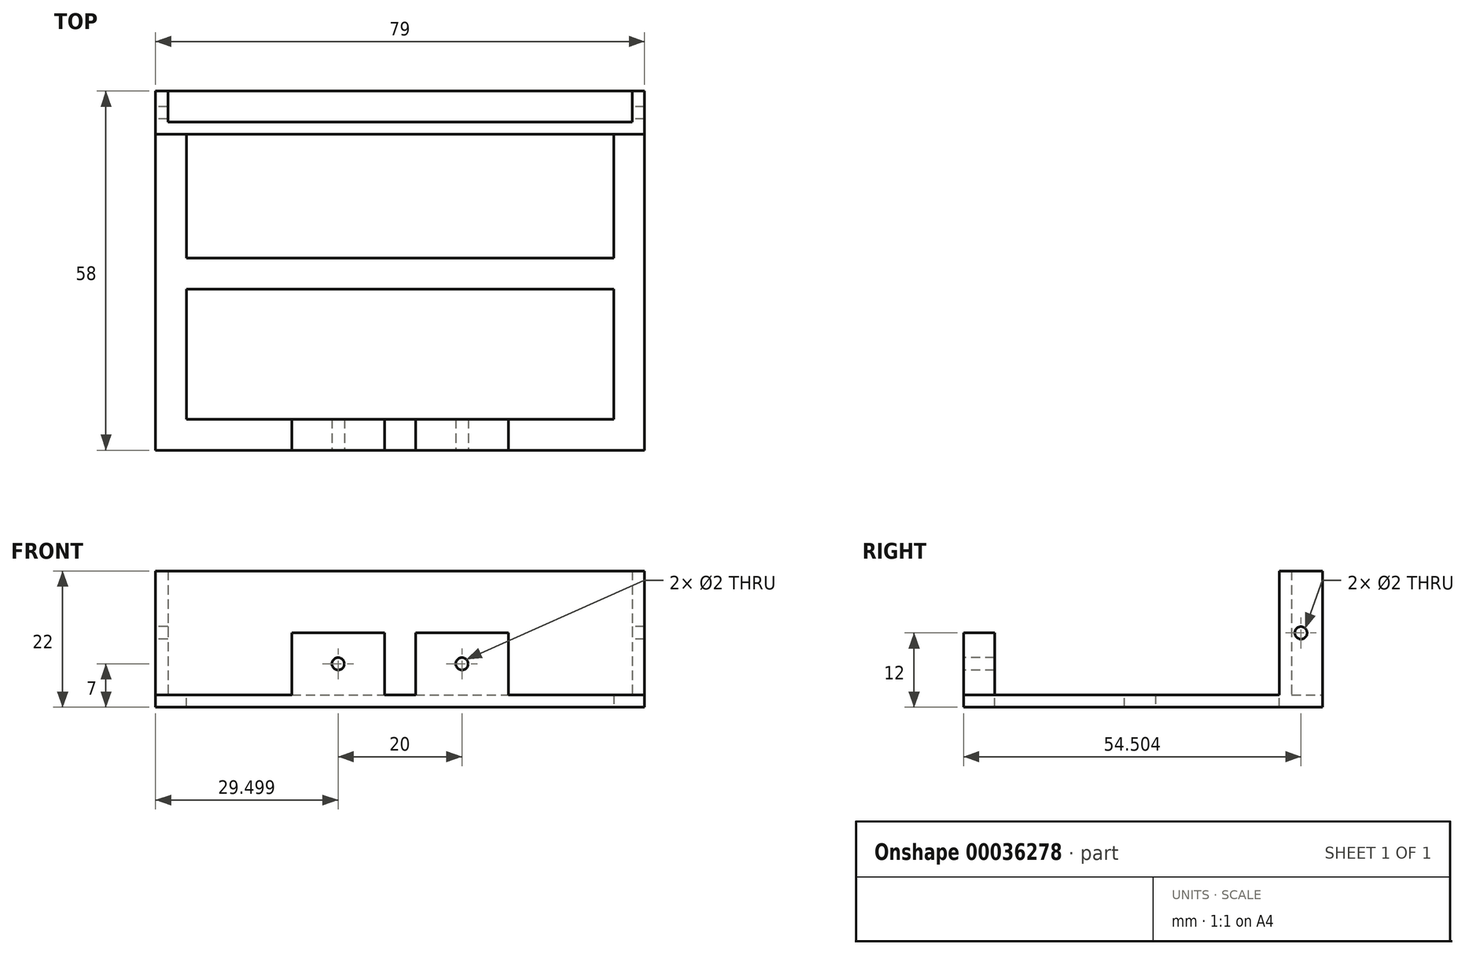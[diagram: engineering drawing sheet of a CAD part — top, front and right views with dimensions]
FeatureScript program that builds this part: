
annotation { "Feature Type Name" : "Feature", "Feature Type Description" : "" }
export const myFeature = defineFeature(function(context is Context, id is Id, definition is map)
    precondition{}
    {
        {
            var Q0;
            Q0=qCreatedBy(makeId("Top.planeOp"),FACE);
            var sketch = newSketch(context, id + "F0", { "sketchPlane" : qUnion([Q0])});
            skLineSegment(sketch, "E0.bottom", {"start": v(-44.08, 15.1) * mm, "end": v(34.92, 15.1) * mm});
            skLineSegment(sketch, "E0.top", {"start": v(-44.08, -42.9) * mm, "end": v(34.92, -42.9) * mm});
            skLineSegment(sketch, "E0.left", {"start": v(-44.08, 15.1) * mm, "end": v(-44.08, -42.9) * mm});
            skLineSegment(sketch, "E0.right", {"start": v(34.92, 15.1) * mm, "end": v(34.92, -42.9) * mm});
            skLineSegment(sketch, "E1.bottom", {"start": v(-39.08, 10.1) * mm, "end": v(29.92, 10.1) * mm});
            skLineSegment(sketch, "E1.top", {"start": v(-39.08, -35.9) * mm, "end": v(29.92, -35.9) * mm});
            skLineSegment(sketch, "E1.left", {"start": v(-39.08, 10.1) * mm, "end": v(-39.08, -35.9) * mm});
            skLineSegment(sketch, "E1.right", {"start": v(29.92, 10.1) * mm, "end": v(29.92, -35.9) * mm});
            skSolve(sketch);
        }
        {
            var Q0;
            Q0=makeQuery(id+"F0.imprint","IMPRINT",FACE,{"disambiguationData":[TD([[makeQuery(id+"F0.imprint","IMPRINT",EDGE,{"derivedFrom":sQuery(id+"F0.wireOp",EDGE,"E0.bottom")}),-1.0]])]});
            extrude(context, id + "F1", {"entities" : qUnion([Q0]), "depth" : 2 * mm});
        }
        {
            var Q0;
            Q0=makeQuery(id+"F1.opExtrude","CAP_FACE",FACE,{"disambiguationData":[OSD([sQuery(id+"F0.wireOp",EDGE,"E0.bottom"),sQuery(id+"F0.wireOp",EDGE,"E0.top"),sQuery(id+"F0.wireOp",EDGE,"E0.left"),sQuery(id+"F0.wireOp",EDGE,"E0.right"),sQuery(id+"F0.wireOp",EDGE,"E1.bottom"),sQuery(id+"F0.wireOp",EDGE,"E1.top"),sQuery(id+"F0.wireOp",EDGE,"E1.left"),sQuery(id+"F0.wireOp",EDGE,"E1.right")])],"isStart":true});
            var sketch = newSketch(context, id + "F2", { "sketchPlane" : qUnion([Q0])});
            skLineSegment(sketch, "E2.bottom", {"start": v(-22.08, -15.1) * mm, "end": v(-7.08, -15.1) * mm});
            skLineSegment(sketch, "E2.top", {"start": v(-22.08, -10.1) * mm, "end": v(-7.08, -10.1) * mm});
            skLineSegment(sketch, "E2.left", {"start": v(-22.08, -15.1) * mm, "end": v(-22.08, -10.1) * mm});
            skLineSegment(sketch, "E2.right", {"start": v(-7.08, -15.1) * mm, "end": v(-7.08, -10.1) * mm});
            skLineSegment(sketch, "E3.bottom", {"start": v(-2.08, -15.1) * mm, "end": v(12.92, -15.1) * mm});
            skLineSegment(sketch, "E3.top", {"start": v(-2.08, -10.1) * mm, "end": v(12.92, -10.1) * mm});
            skLineSegment(sketch, "E3.left", {"start": v(-2.08, -15.1) * mm, "end": v(-2.08, -10.1) * mm});
            skLineSegment(sketch, "E3.right", {"start": v(12.92, -15.1) * mm, "end": v(12.92, -10.1) * mm});
            skSolve(sketch);
        }
        {
            var Q0;
            Q0=makeQuery(id+"F2.imprint","IMPRINT",FACE,{"disambiguationData":[TD([[makeQuery(id+"F2.imprint","IMPRINT",EDGE,{"derivedFrom":sQuery(id+"F2.wireOp",EDGE,"E3.bottom")}),1.0]])]});
            var Q1;
            Q1=makeQuery(id+"F2.imprint","IMPRINT",FACE,{"disambiguationData":[TD([[makeQuery(id+"F2.imprint","IMPRINT",EDGE,{"derivedFrom":sQuery(id+"F2.wireOp",EDGE,"E2.bottom")}),1.0]])]});
            extrude(context, id + "F3", {"entities" : qUnion([Q0, Q1]), "operationType" : NewBodyOperationType.ADD, "depth" : 10 * mm});
        }
        {
            var Q0;
            {var subQ0=sQuery(id+"F0.wireOp",EDGE,"E0.bottom");var subQ1=sQuery(id+"F0.wireOp",EDGE,"E0.top");var subQ2=sQuery(id+"F0.wireOp",EDGE,"E0.left");var subQ3=sQuery(id+"F0.wireOp",EDGE,"E0.right");var subQ4=sQuery(id+"F0.wireOp",EDGE,"E1.bottom");var subQ5=sQuery(id+"F0.wireOp",EDGE,"E1.top");var subQ6=sQuery(id+"F0.wireOp",EDGE,"E1.left");var subQ7=sQuery(id+"F0.wireOp",EDGE,"E1.right");Q0=makeQuery(id+"F3.boolean.opBoolean","SPLIT",FACE,{"disambiguationData":[TD([makeQuery(id+"F1.opExtrude","SWEPT_FACE",FACE,{"disambiguationData":[OSD([subQ1])]})])],"derivedFrom":makeQuery(id+"F1.opExtrude","CAP_FACE",FACE,{"disambiguationData":[OSD([subQ0,subQ1,subQ2,subQ3,subQ4,subQ5,subQ6,subQ7])],"isStart":true})});}
            var sketch = newSketch(context, id + "F4", { "sketchPlane" : qUnion([Q0])});
            skLineSegment(sketch, "E4.bottom", {"start": v(34.92, 42.9) * mm, "end": v(-44.08, 42.9) * mm});
            skLineSegment(sketch, "E4.top", {"start": v(34.92, 35.9) * mm, "end": v(-44.08, 35.9) * mm});
            skLineSegment(sketch, "E4.left", {"start": v(34.92, 42.9) * mm, "end": v(34.92, 35.9) * mm});
            skLineSegment(sketch, "E4.right", {"start": v(-44.08, 42.9) * mm, "end": v(-44.08, 35.9) * mm});
            skSolve(sketch);
        }
        {
            var Q0;
            Q0=makeQuery(id+"F4.imprint","IMPRINT",FACE,{"disambiguationData":[TD([[makeQuery(id+"F4.imprint","IMPRINT",EDGE,{"derivedFrom":sQuery(id+"F4.wireOp",EDGE,"E4.bottom")}),-1.0]])]});
            extrude(context, id + "F5", {"entities" : qUnion([Q0]), "operationType" : NewBodyOperationType.ADD, "depth" : 20 * mm});
        }
        {
            var Q0;
            Q0=makeQuery(id+"F5.boolean.opBoolean","MERGE",FACE,{"derivedFrom":[makeQuery(id+"F1.opExtrude","SWEPT_FACE",FACE,{"disambiguationData":[OSD([sQuery(id+"F0.wireOp",EDGE,"E0.top")])]}),makeQuery(id+"F5.opExtrude","SWEPT_FACE",FACE,{"disambiguationData":[OSD([sQuery(id+"F4.wireOp",EDGE,"E4.bottom")])]})]});
            var sketch = newSketch(context, id + "F6", { "sketchPlane" : qUnion([Q0])});
            skLineSegment(sketch, "E5.bottom", {"start": v(-42.08, -20) * mm, "end": v(32.92, -20) * mm});
            skLineSegment(sketch, "E5.top", {"start": v(-42.08, 0) * mm, "end": v(32.92, 0) * mm});
            skLineSegment(sketch, "E5.left", {"start": v(-42.08, -20) * mm, "end": v(-42.08, 0) * mm});
            skLineSegment(sketch, "E5.right", {"start": v(32.92, -20) * mm, "end": v(32.92, 0) * mm});
            skSolve(sketch);
        }
        {
            var Q0;
            Q0=makeQuery(id+"F6.imprint","IMPRINT",FACE,{"disambiguationData":[TD([[makeQuery(id+"F6.imprint","IMPRINT",EDGE,{"derivedFrom":sQuery(id+"F6.wireOp",EDGE,"E5.bottom")}),1.0]])]});
            extrude(context, id + "F7", {"entities" : qUnion([Q0]), "operationType" : NewBodyOperationType.REMOVE, "oppositeDirection" : true, "depth" : 5 * mm});
        }
        {
            var Q0;
            Q0=makeQuery(id+"F3.boolean.opBoolean","MERGE",FACE,{"derivedFrom":[makeQuery(id+"F1.opExtrude","SWEPT_FACE",FACE,{"disambiguationData":[OSD([sQuery(id+"F0.wireOp",EDGE,"E0.bottom")])]}),makeQuery(id+"F3.opExtrude","SWEPT_FACE",FACE,{"disambiguationData":[OSD([sQuery(id+"F2.wireOp",EDGE,"E2.bottom")])]}),makeQuery(id+"F3.opExtrude","SWEPT_FACE",FACE,{"disambiguationData":[OSD([sQuery(id+"F2.wireOp",EDGE,"E3.bottom")])]})]});
            var sketch = newSketch(context, id + "F8", { "sketchPlane" : qUnion([Q0])});
            skLineSegment(sketch, "E6", {"start": v(-12.92, -5) * mm, "end": v(2.08, -5) * mm, "construction": true});
            skLineSegment(sketch, "E7", {"start": v(-5.42, -10) * mm, "end": v(-5.42, -5) * mm, "construction": true});
            skLineSegment(sketch, "E8", {"start": v(-5.42, -5) * mm, "end": v(-5.42, 0) * mm, "construction": true});
            skLineSegment(sketch, "E9", {"start": v(7.08, -5) * mm, "end": v(22.08, -5) * mm, "construction": true});
            skLineSegment(sketch, "E10", {"start": v(14.58, -10) * mm, "end": v(14.58, -5) * mm, "construction": true});
            skLineSegment(sketch, "E11", {"start": v(14.58, -5) * mm, "end": v(14.58, 0) * mm, "construction": true});
            skCircle(sketch, "E12", {"center": v(-5.42, -5) * mm, "radius": 1 * mm});
            skCircle(sketch, "E13", {"center": v(14.58, -5) * mm, "radius": 1 * mm});
            skSolve(sketch);
        }
        {
            var Q0;
            Q0=makeQuery(id+"F8.imprint","IMPRINT",FACE,{"disambiguationData":[TD([[makeQuery(id+"F8.imprint","IMPRINT",EDGE,{"derivedFrom":sQuery(id+"F8.wireOp",EDGE,"E12")}),1.0]])]});
            var Q1;
            Q1=makeQuery(id+"F8.imprint","IMPRINT",FACE,{"disambiguationData":[TD([[makeQuery(id+"F8.imprint","IMPRINT",EDGE,{"derivedFrom":sQuery(id+"F8.wireOp",EDGE,"E13")}),1.0]])]});
            extrude(context, id + "F9", {"entities" : qUnion([Q0, Q1]), "operationType" : NewBodyOperationType.REMOVE, "endBound" : BoundingType.UP_TO_NEXT, "oppositeDirection" : true, "depth" : 25 * mm});
        }
        {
            var Q0;
            Q0=makeQuery(id+"F5.boolean.opBoolean","MERGE",FACE,{"derivedFrom":[makeQuery(id+"F1.opExtrude","SWEPT_FACE",FACE,{"disambiguationData":[OSD([sQuery(id+"F0.wireOp",EDGE,"E0.left")])]}),makeQuery(id+"F5.opExtrude","SWEPT_FACE",FACE,{"disambiguationData":[OSD([sQuery(id+"F4.wireOp",EDGE,"E4.right")])]})]});
            var sketch = newSketch(context, id + "F10", { "sketchPlane" : qUnion([Q0])});
            skLineSegment(sketch, "E14", {"start": v(39.4, -20) * mm, "end": v(39.4, 0) * mm, "construction": true});
            skLineSegment(sketch, "E15", {"start": v(35.9, -10) * mm, "end": v(39.4, -10) * mm, "construction": true});
            skLineSegment(sketch, "E16", {"start": v(39.4, -10) * mm, "end": v(42.9, -10) * mm, "construction": true});
            skCircle(sketch, "E17", {"center": v(39.4, -10) * mm, "radius": 1 * mm});
            skSolve(sketch);
        }
        {
            var Q0;
            Q0=makeQuery(id+"F10.imprint","IMPRINT",FACE,{"disambiguationData":[TD([[makeQuery(id+"F10.imprint","IMPRINT",EDGE,{"derivedFrom":sQuery(id+"F10.wireOp",EDGE,"E17")}),1.0]])]});
            extrude(context, id + "F11", {"entities" : qUnion([Q0]), "operationType" : NewBodyOperationType.REMOVE, "endBound" : BoundingType.THROUGH_ALL, "oppositeDirection" : true, "depth" : 25 * mm});
        }
        {
            var Q0;
            Q0=makeQuery(id+"F1.opExtrude","SWEPT_FACE",FACE,{"disambiguationData":[OSD([sQuery(id+"F0.wireOp",EDGE,"E1.right")])]});
            var sketch = newSketch(context, id + "F12", { "sketchPlane" : qUnion([Q0])});
            skLineSegment(sketch, "E18.bottom", {"start": v(10.9, 0) * mm, "end": v(15.9, 0) * mm});
            skLineSegment(sketch, "E18.top", {"start": v(10.9, 2) * mm, "end": v(15.9, 2) * mm});
            skLineSegment(sketch, "E18.left", {"start": v(10.9, 0) * mm, "end": v(10.9, 2) * mm});
            skLineSegment(sketch, "E18.right", {"start": v(15.9, 0) * mm, "end": v(15.9, 2) * mm});
            skSolve(sketch);
        }
        {
            var Q0;
            Q0=makeQuery(id+"F12.imprint","IMPRINT",FACE,{"disambiguationData":[TD([[makeQuery(id+"F12.imprint","IMPRINT",EDGE,{"derivedFrom":sQuery(id+"F12.wireOp",EDGE,"E18.bottom")}),1.0]])]});
            extrude(context, id + "F13", {"entities" : qUnion([Q0]), "operationType" : NewBodyOperationType.ADD, "endBound" : BoundingType.UP_TO_NEXT, "depth" : 25 * mm});
        }
        {
            var Q0;
            Q0=makeQuery(id+"F1.opExtrude","SWEPT_BODY",BODY,{"disambiguationData":[OSD([sQuery(id+"F0.wireOp",EDGE,"E0.bottom"),sQuery(id+"F0.wireOp",EDGE,"E0.top"),sQuery(id+"F0.wireOp",EDGE,"E0.left"),sQuery(id+"F0.wireOp",EDGE,"E0.right"),sQuery(id+"F0.wireOp",EDGE,"E1.bottom"),sQuery(id+"F0.wireOp",EDGE,"E1.top"),sQuery(id+"F0.wireOp",EDGE,"E1.left"),sQuery(id+"F0.wireOp",EDGE,"E1.right")])]});
            var Q1;
            Q1=makeQuery(id+"F13.opExtrude","SWEPT_EDGE",EDGE,{"disambiguationData":[OSD([sQuery(id+"F0.wireOp",EDGE,"E1.right"),sQuery(id+"F12.wireOp",EDGE,"E18.top"),sQuery(id+"F12.wireOp",EDGE,"E18.left")])]});
            transform(context, id + "F14", {"entities" : qUnion([Q0]), "transformType" : TransformType.ROTATION, "transformAxis" : qUnion([Q1]), "angle" : 180 * degree, "makeCopy" : false});
        }
    });
